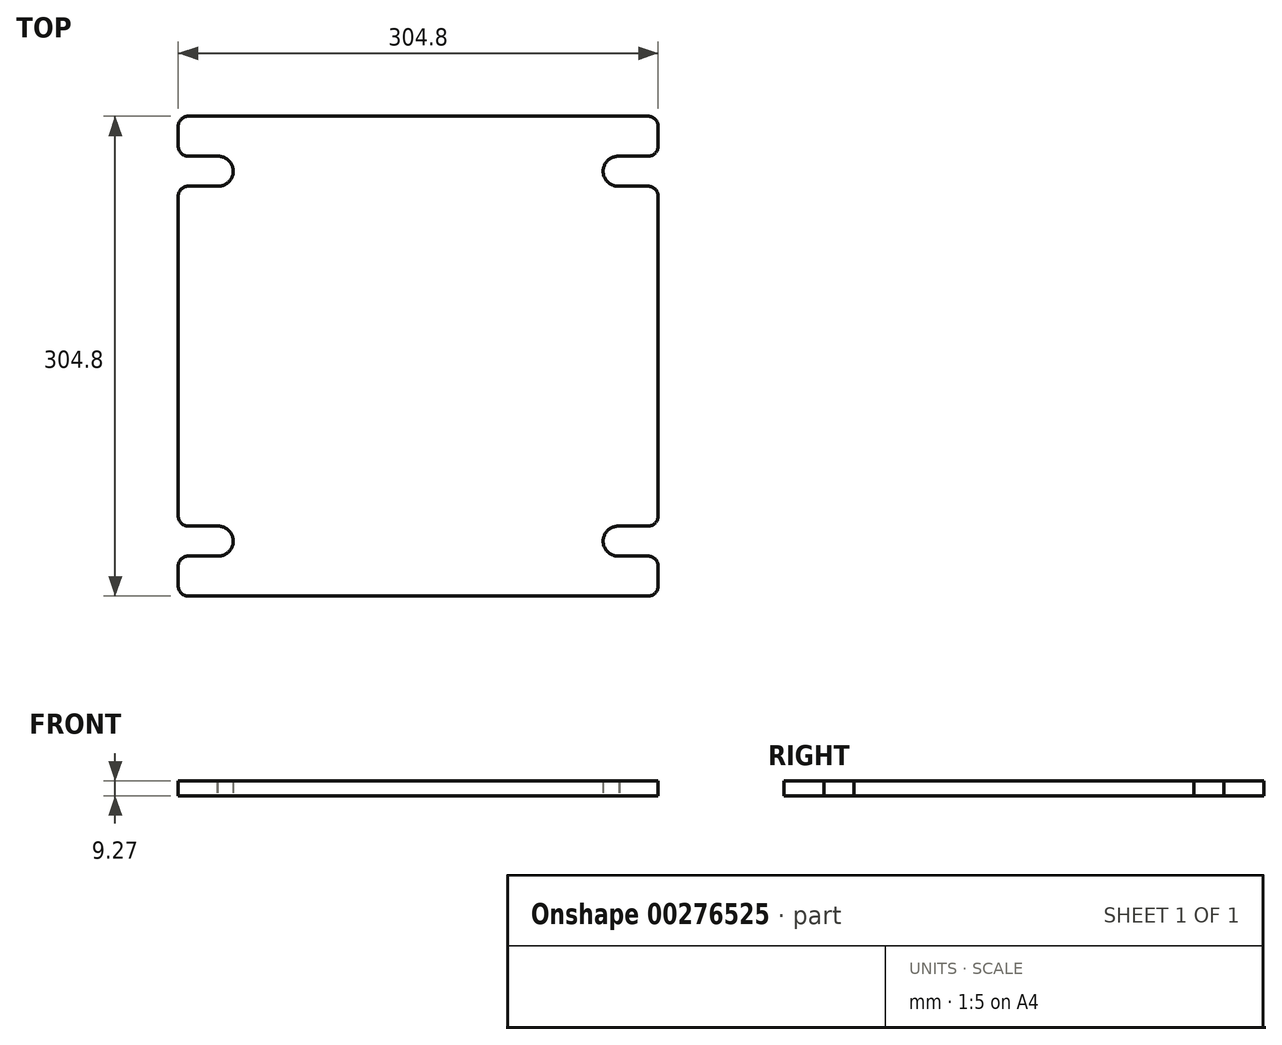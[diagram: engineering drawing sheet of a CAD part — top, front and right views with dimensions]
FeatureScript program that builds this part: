
annotation { "Feature Type Name" : "Feature", "Feature Type Description" : "" }
export const myFeature = defineFeature(function(context is Context, id is Id, definition is map)
    precondition{}
    {
        {
            var Q0;
            Q0=qCreatedBy(makeId("Top.planeOp"),FACE);
            var sketch = newSketch(context, id + "F0", { "sketchPlane" : qUnion([Q0])});
            skLineSegment(sketch, "E0.bottom", {"start": v(0, -152.4) * mm, "end": v(-152.4, -152.4) * mm});
            skLineSegment(sketch, "E0.top", {"start": v(0, 152.4) * mm, "end": v(-152.4, 152.4) * mm});
            skLineSegment(sketch, "E0.right", {"start": v(-152.4, -152.4) * mm, "end": v(-152.4, -126.97) * mm});
            skPoint(sketch, "E0.middle", {"position": v(0, 0) * mm});
            skArc(sketch, "E1", {"start": v(-127.76, 107.98) * mm, "mid": v(-117.48, 117.35) * mm, "end": v(-127.5, 126.99) * mm});
            skLineSegment(sketch, "E2", {"start": v(-127.5, 126.99) * mm, "end": v(-152.4, 126.99) * mm});
            skLineSegment(sketch, "E3", {"start": v(-127.76, 107.98) * mm, "end": v(-152.4, 107.98) * mm});
            skLineSegment(sketch, "E4.trimOffspring", {"start": v(-152.4, 126.99) * mm, "end": v(-152.4, 152.4) * mm});
            skArc(sketch, "E5", {"start": v(-127.76, -126.97) * mm, "mid": v(-117.48, -117.6) * mm, "end": v(-127.5, -107.96) * mm});
            skLineSegment(sketch, "E6", {"start": v(-127.5, -107.96) * mm, "end": v(-152.4, -107.96) * mm});
            skLineSegment(sketch, "E7", {"start": v(-127.76, -126.97) * mm, "end": v(-152.4, -126.97) * mm});
            skLineSegment(sketch, "E8.trimOffspring", {"start": v(-152.4, -107.96) * mm, "end": v(-152.4, 107.98) * mm});
            skLineSegment(sketch, "E9", {"start": v(0, 186.07) * mm, "end": v(0, -165.08) * mm, "construction": true});
            skPoint(sketch, "E9.startSnap0", {"position": v(0, 152.4) * mm});
            skPoint(sketch, "E9.endSnap0", {"position": v(0, -152.4) * mm});
            skLineSegment(sketch, "E10.MirrorCS", {"start": v(0, 152.4) * mm, "end": v(152.4, 152.4) * mm});
            skLineSegment(sketch, "E11.MirrorCS", {"start": v(152.4, -152.4) * mm, "end": v(152.4, -126.97) * mm});
            skArc(sketch, "E12.MirrorCS", {"start": v(127.76, 107.98) * mm, "mid": v(117.48, 117.35) * mm, "end": v(127.5, 126.99) * mm});
            skLineSegment(sketch, "E13.MirrorCS", {"start": v(152.4, -107.96) * mm, "end": v(152.4, 107.98) * mm});
            skLineSegment(sketch, "E14.MirrorCS", {"start": v(127.5, -107.96) * mm, "end": v(152.4, -107.96) * mm});
            skLineSegment(sketch, "E15.MirrorCS", {"start": v(127.76, 107.98) * mm, "end": v(152.4, 107.98) * mm});
            skLineSegment(sketch, "E16.MirrorCS", {"start": v(152.4, 126.99) * mm, "end": v(152.4, 152.4) * mm});
            skLineSegment(sketch, "E17.MirrorCS", {"start": v(127.76, -126.97) * mm, "end": v(152.4, -126.97) * mm});
            skLineSegment(sketch, "E18.MirrorCS", {"start": v(127.5, 126.99) * mm, "end": v(152.4, 126.99) * mm});
            skLineSegment(sketch, "E19.MirrorCS", {"start": v(0, -152.4) * mm, "end": v(152.4, -152.4) * mm});
            skArc(sketch, "E20.MirrorCS", {"start": v(127.76, -126.97) * mm, "mid": v(117.48, -117.6) * mm, "end": v(127.5, -107.96) * mm});
            skSolve(sketch);
        }
        {
            var Q0;
            Q0 = qSketchRegion(id + "F0", true);
            extrude(context, id + "F1", {"entities" : qUnion([Q0]), "depth" : 9.27 * mm});
        }
        {
            var Q0;
            Q0=makeQuery(id+"F1.opExtrude","SWEPT_EDGE",EDGE,{"disambiguationData":[OSD([sQuery(id+"F0.wireOp",EDGE,"E0.top"),sQuery(id+"F0.wireOp",EDGE,"E4.trimOffspring")])]});
            var Q1;
            Q1=makeQuery(id+"F1.opExtrude","SWEPT_EDGE",EDGE,{"disambiguationData":[OSD([sQuery(id+"F0.wireOp",EDGE,"E10.MirrorCS"),sQuery(id+"F0.wireOp",EDGE,"E16.MirrorCS")])]});
            var Q2;
            Q2=makeQuery(id+"F1.opExtrude","SWEPT_EDGE",EDGE,{"disambiguationData":[OSD([sQuery(id+"F0.wireOp",EDGE,"E11.MirrorCS"),sQuery(id+"F0.wireOp",EDGE,"E19.MirrorCS")])]});
            var Q3;
            Q3=makeQuery(id+"F1.opExtrude","SWEPT_EDGE",EDGE,{"disambiguationData":[OSD([sQuery(id+"F0.wireOp",EDGE,"E0.bottom"),sQuery(id+"F0.wireOp",EDGE,"E0.right")])]});
            var Q4;
            Q4=makeQuery(id+"F1.opExtrude","SWEPT_EDGE",EDGE,{"disambiguationData":[OSD([sQuery(id+"F0.wireOp",EDGE,"E11.MirrorCS"),sQuery(id+"F0.wireOp",EDGE,"E17.MirrorCS")])]});
            var Q5;
            Q5=makeQuery(id+"F1.opExtrude","SWEPT_EDGE",EDGE,{"disambiguationData":[OSD([sQuery(id+"F0.wireOp",EDGE,"E13.MirrorCS"),sQuery(id+"F0.wireOp",EDGE,"E14.MirrorCS")])]});
            var Q6;
            Q6=makeQuery(id+"F1.opExtrude","SWEPT_EDGE",EDGE,{"disambiguationData":[OSD([sQuery(id+"F0.wireOp",EDGE,"E13.MirrorCS"),sQuery(id+"F0.wireOp",EDGE,"E15.MirrorCS")])]});
            var Q7;
            Q7=makeQuery(id+"F1.opExtrude","SWEPT_EDGE",EDGE,{"disambiguationData":[OSD([sQuery(id+"F0.wireOp",EDGE,"E16.MirrorCS"),sQuery(id+"F0.wireOp",EDGE,"E18.MirrorCS")])]});
            var Q8;
            Q8=makeQuery(id+"F1.opExtrude","SWEPT_EDGE",EDGE,{"disambiguationData":[OSD([sQuery(id+"F0.wireOp",EDGE,"E6"),sQuery(id+"F0.wireOp",EDGE,"E8.trimOffspring")])]});
            var Q9;
            Q9=makeQuery(id+"F1.opExtrude","SWEPT_EDGE",EDGE,{"disambiguationData":[OSD([sQuery(id+"F0.wireOp",EDGE,"E2"),sQuery(id+"F0.wireOp",EDGE,"E4.trimOffspring")])]});
            var Q10;
            Q10=makeQuery(id+"F1.opExtrude","SWEPT_EDGE",EDGE,{"disambiguationData":[OSD([sQuery(id+"F0.wireOp",EDGE,"E0.right"),sQuery(id+"F0.wireOp",EDGE,"E7")])]});
            var Q11;
            Q11=makeQuery(id+"F1.opExtrude","SWEPT_EDGE",EDGE,{"disambiguationData":[OSD([sQuery(id+"F0.wireOp",EDGE,"E3"),sQuery(id+"F0.wireOp",EDGE,"E8.trimOffspring")])]});
            fillet(context, id + "F2", {"entities" : qUnion([Q0, Q1, Q2, Q3, Q4, Q5, Q6, Q7, Q8, Q9, Q10, Q11]), "radius" : 6.35 * mm, "tangentPropagation" : true, "allowEdgeOverflow" : false});
        }
    });
